# Revit family: Camera-Security-Panasonic-HD-Vandal_Resistant-Wall_Mount-Network-SW115
name_source: partatom
category: Security Devices
revit_build: Autodesk Revit 2013 (Build: 20130531_2115(x64)
units: mm (PartAtom-declared; Revit-internal decimal feet)

## types (1)
- HD, Vandal Resistant, Wall Mount, Network, SW115
    Angle Of View = 104
    Audio In = None
    Audio Out = None
    Auto Back Focus = No
    Communication Ports = 10Base-T / 100Base-TX, RJ-45
    Date Last Modified = March, 6, 2015
    Day Or Night = Yes
    Depth = 1.929 "
    Description = Security Camera, Vandal Resistant, Wall Mount, Network, Super Dynamic, HD
    Equipment Abbreviation = SC
    Family Version = 1.0.0
    Has POE = Yes
    Height = 3.425 "
    IP Or Analog = IP
    Indoor Or Outdoor = Outdoor
    Manufacturer = Panasonic
    Minimum Illumination = 1 lx
    Model = WV-SW115
    Model Disclaimer = Contact Panasonic for more information
    Mounting Positions = Surface Mount
    Operational Humidity = 20% to 90% (no condensation)
    Operational Temperature = -22°F - 122°F
    Part Description = Security Camera, Vandal Resistant, Wall Mount, Network, Super Dynamic, HD
    Part Number = WV-SW115
    Product Documentation Link = http://ssbu-t.psn-web.net
    Product Material = Paint - Panasonic - Silver
    Product Page URL = http://security.panasonic.com
    Provide Feedback = https://www.surveymonkey.com
    Rated Current = 56.00 mA
    Regulatory Compliance = UL 60950-1, FCC Part 15 Class A, C-UL, CAN/CSAC22.2 No.60950-1, ICES 003 Class A
    Storage Temperature = -22°F - 122°F
    URL = http://security.panasonic.com
    Vandal Resistant = Yes
    Voltage DC = 48 V
    Weight = 0.88 lb
    Wide Dynamic Range (Super Dynamic) = Yes
    Width = 4.764 "

## geometry (parser evidence)
native form markers: Sweep x3
no freeform markers — native parametric forms only
